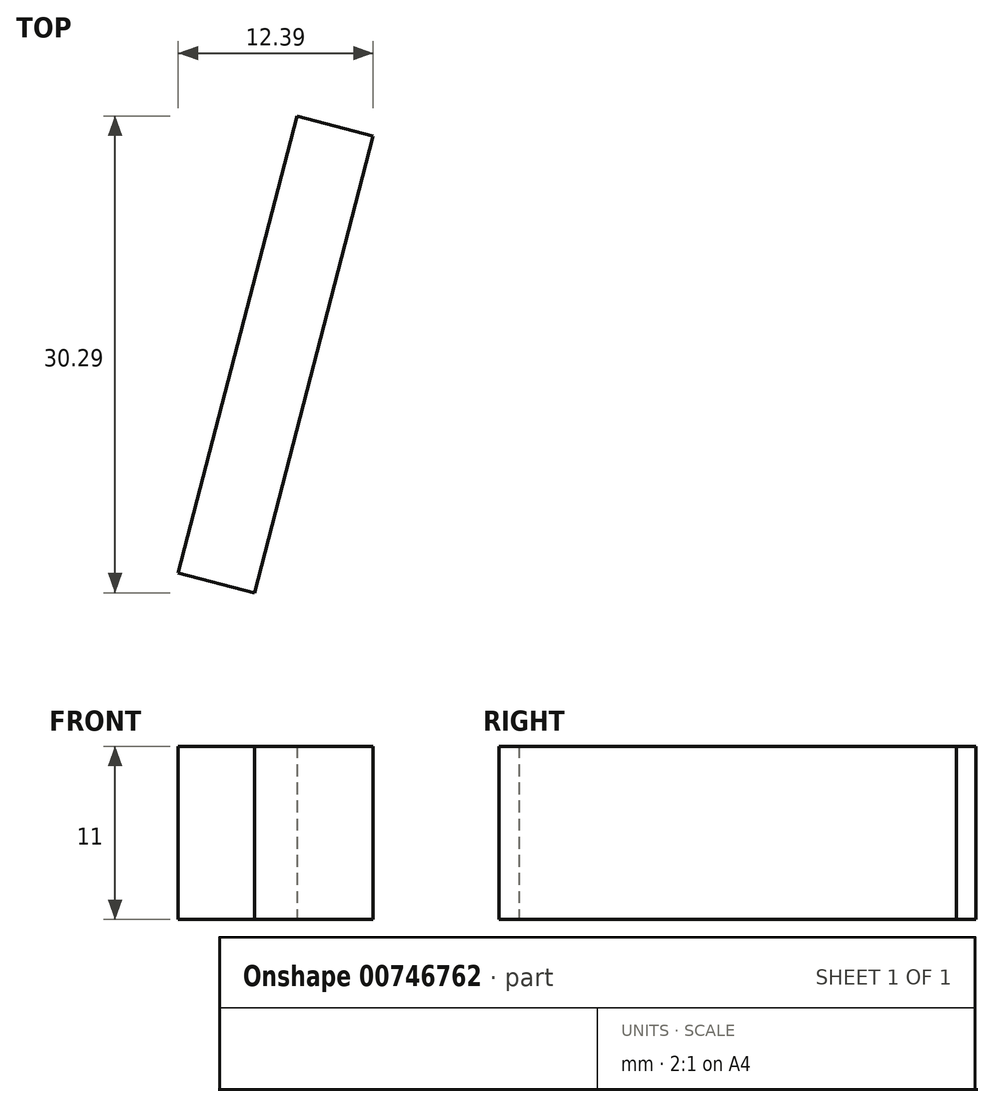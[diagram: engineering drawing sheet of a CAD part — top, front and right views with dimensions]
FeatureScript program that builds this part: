
annotation { "Feature Type Name" : "Feature", "Feature Type Description" : "" }
export const myFeature = defineFeature(function(context is Context, id is Id, definition is map)
    precondition{}
    {
        {
            var Q0;
            Q0=qCreatedBy(makeId("Top.planeOp"),FACE);
            var sketch = newSketch(context, id + "F0", { "sketchPlane" : qUnion([Q0])});
            skLineSegment(sketch, "E0", {"start": v(2.71, 16.95) * mm, "end": v(-4.84, -12.08) * mm});
            skLineSegment(sketch, "E1", {"start": v(-4.84, -12.08) * mm, "end": v(0, -13.34) * mm});
            skLineSegment(sketch, "E2", {"start": v(0, -13.34) * mm, "end": v(7.55, 15.69) * mm});
            skLineSegment(sketch, "E3", {"start": v(7.55, 15.69) * mm, "end": v(2.71, 16.95) * mm});
            skSolve(sketch);
        }
        {
            var Q0;
            Q0=makeQuery(id+"F0.imprint","IMPRINT",FACE,{"disambiguationData":[TD([[makeQuery(id+"F0.imprint","IMPRINT",EDGE,{"derivedFrom":sQuery(id+"F0.wireOp",EDGE,"E0")}),1.0]])]});
            extrude(context, id + "F1", {"entities" : qUnion([Q0]), "depth" : 11 * mm, "offsetDistance" : 25 * mm});
        }
    });
